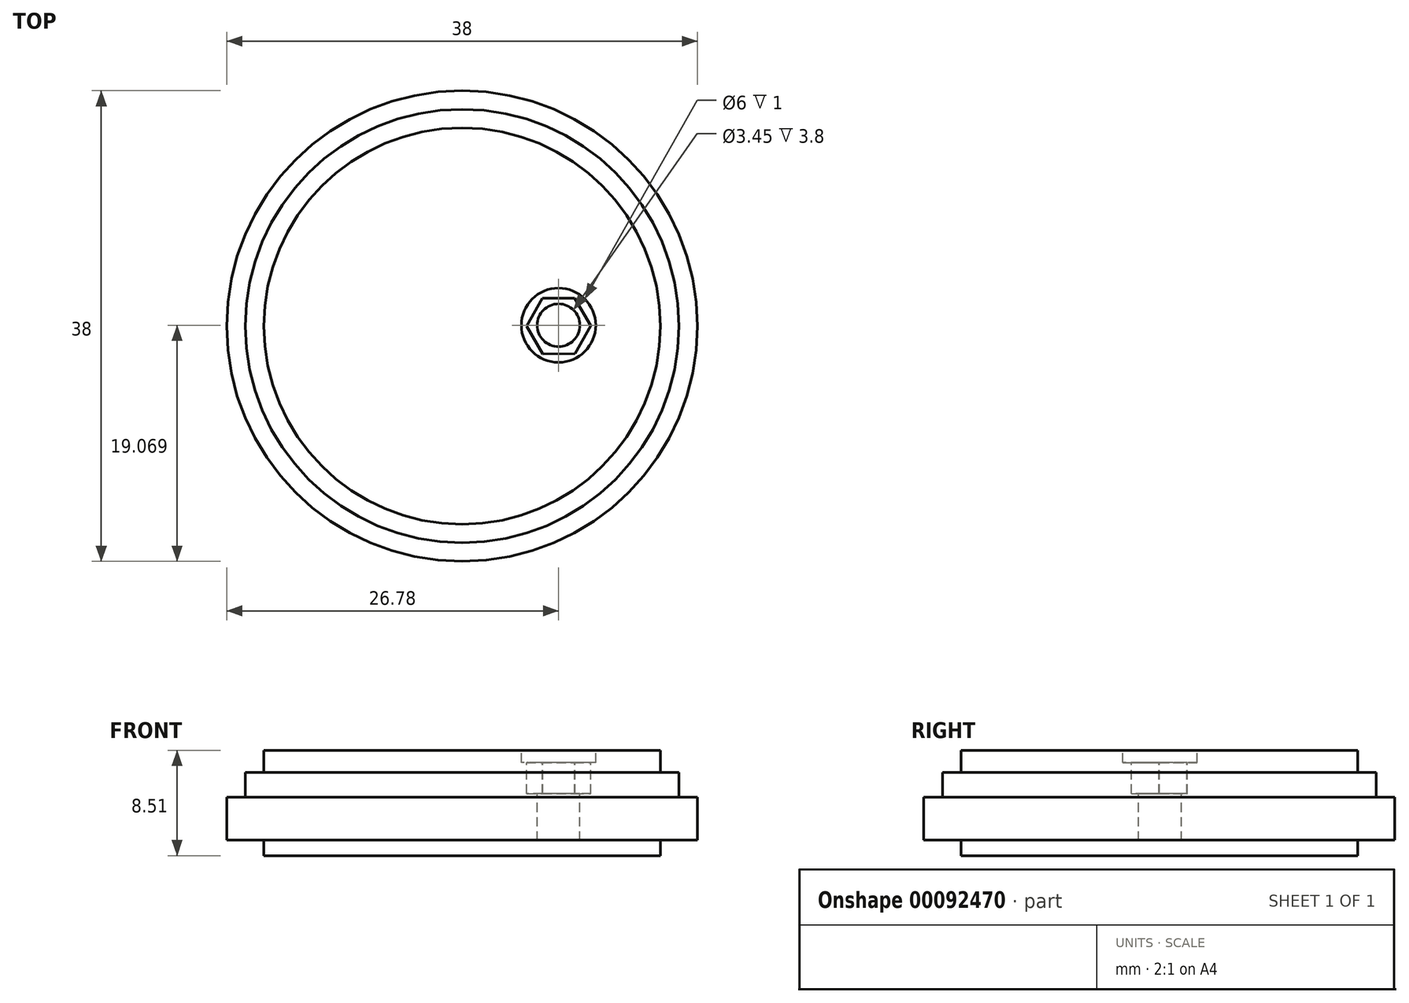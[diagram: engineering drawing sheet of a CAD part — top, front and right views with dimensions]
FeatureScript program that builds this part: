
annotation { "Feature Type Name" : "Feature", "Feature Type Description" : "" }
export const myFeature = defineFeature(function(context is Context, id is Id, definition is map)
    precondition{}
    {
        {
            var Q0;
            Q0=qCreatedBy(makeId("Front.planeOp"),FACE);
            var sketch = newSketch(context, id + "F0", { "sketchPlane" : qUnion([Q0])});
            skLineSegment(sketch, "E0", {"start": v(-26.8, 0) * mm, "end": v(11.2, 0) * mm});
            skLineSegment(sketch, "E1", {"start": v(11.2, 0) * mm, "end": v(11.2, 3.46) * mm});
            skLineSegment(sketch, "E2", {"start": v(11.2, 3.46) * mm, "end": v(9.7, 3.46) * mm});
            skLineSegment(sketch, "E3", {"start": v(9.7, 3.46) * mm, "end": v(9.7, 5.47) * mm});
            skLineSegment(sketch, "E4", {"start": v(9.7, 5.47) * mm, "end": v(8.2, 5.47) * mm});
            skLineSegment(sketch, "E5", {"start": v(8.2, 5.47) * mm, "end": v(8.2, 7.26) * mm});
            skLineSegment(sketch, "E6", {"start": v(8.2, 7.26) * mm, "end": v(-23.8, 7.26) * mm});
            skLineSegment(sketch, "E7", {"start": v(-23.8, 7.26) * mm, "end": v(-23.8, 5.47) * mm});
            skLineSegment(sketch, "E8", {"start": v(-23.8, 5.47) * mm, "end": v(-25.3, 5.47) * mm});
            skLineSegment(sketch, "E9", {"start": v(-25.3, 5.47) * mm, "end": v(-25.3, 3.46) * mm});
            skLineSegment(sketch, "E10", {"start": v(-25.3, 3.46) * mm, "end": v(-26.8, 3.46) * mm});
            skLineSegment(sketch, "E11", {"start": v(-26.8, 3.46) * mm, "end": v(-26.8, 0) * mm});
            skLineSegment(sketch, "E12", {"start": v(-23.8, 0) * mm, "end": v(-23.8, -1.25) * mm});
            skLineSegment(sketch, "E13", {"start": v(-23.8, -1.25) * mm, "end": v(8.2, -1.25) * mm});
            skLineSegment(sketch, "E14", {"start": v(8.2, -1.25) * mm, "end": v(8.2, 0) * mm});
            skLineSegment(sketch, "E15", {"start": v(-7.8, -4.04) * mm, "end": v(-7.8, 9.51) * mm});
            skPoint(sketch, "E15.startSnap0", {"position": v(-7.8, 0) * mm});
            skSolve(sketch);
        }
        {
            var Q0;
            {var subQ0=sQuery(id+"F0.wireOp",EDGE,"E1");Q0=makeQuery(id+"F0.imprint","IMPRINT",FACE,{"disambiguationData":[TD([[makeQuery(id+"F0.imprint","IMPRINT",EDGE,{"derivedFrom":subQ0}),1.0]])]});}
            var Q1;
            {var subQ0=sQuery(id+"F0.wireOp",EDGE,"E14");Q1=makeQuery(id+"F0.imprint","IMPRINT",FACE,{"disambiguationData":[TD([[makeQuery(id+"F0.imprint","IMPRINT",EDGE,{"derivedFrom":subQ0}),1.0]])]});}
            var Q2;
            Q2=sQuery(id+"F0.wireOp",EDGE,"E15");
            revolve(context, id + "F1", {"entities" : qUnion([Q0, Q1]), "axis" : qUnion([Q2]), "revolveType" : RevolveType.FULL});
        }
        {
            var Q0;
            Q0=makeQuery(id+"F1.opRevolve","SWEPT_FACE",FACE,{"disambiguationData":[OSD([sQuery(id+"F0.wireOp",EDGE,"E6")])]});
            cPlane(context, id + "F2", {"entities" : qUnion([Q0]), "cplaneType" : CPlaneType.OFFSET, "offset" : 0 * mm, "width" : 150 * mm, "height" : 150 * mm});
        }
        {
            var Q0;
            Q0=qCreatedBy(id+"F2.planeOp",FACE);
            var sketch = newSketch(context, id + "F3", { "sketchPlane" : qUnion([Q0])});
            skCircle(sketch, "E16", {"center": v(-0.01, 0.07) * mm, "radius": 3 * mm});
            skCircle(sketch, "E17", {"center": v(-0.01, 0.07) * mm, "radius": 1.73 * mm});
            skCircle(sketch, "E18.cCircle", {"center": v(0, 0) * mm, "radius": 2.25 * mm, "construction": true});
            skLineSegment(sketch, "E18.0", {"start": v(-2.6, -0.02) * mm, "end": v(-1.31, 2.24) * mm});
            skLineSegment(sketch, "E18.1", {"start": v(-1.31, 2.24) * mm, "end": v(1.28, 2.26) * mm});
            skLineSegment(sketch, "E18.2", {"start": v(1.28, 2.26) * mm, "end": v(2.6, 0.02) * mm});
            skLineSegment(sketch, "E18.3", {"start": v(2.6, 0.02) * mm, "end": v(1.31, -2.24) * mm});
            skLineSegment(sketch, "E18.4", {"start": v(1.31, -2.24) * mm, "end": v(-1.28, -2.26) * mm});
            skLineSegment(sketch, "E18.5", {"start": v(-1.28, -2.26) * mm, "end": v(-2.6, -0.02) * mm});
            skPoint(sketch, "E18.0.midPoint", {"position": v(-1.96, 1.11) * mm});
            skSolve(sketch);
        }
        {
            var Q0;
            Q0=makeQuery(id+"F3.imprint","IMPRINT",FACE,{"disambiguationData":[TD([[makeQuery(id+"F3.imprint","IMPRINT",EDGE,{"derivedFrom":sQuery(id+"F3.wireOp",EDGE,"E17")}),1.0]])]});
            extrude(context, id + "F4", {"entities" : qUnion([Q0]), "operationType" : NewBodyOperationType.REMOVE, "oppositeDirection" : true, "depth" : 7.3 * mm});
        }
        {
            var Q0;
            Q0=makeQuery(id+"F3.imprint","IMPRINT",FACE,{"disambiguationData":[TD([[makeQuery(id+"F3.imprint","IMPRINT",EDGE,{"derivedFrom":sQuery(id+"F3.wireOp",EDGE,"E17")}),-1.0]])]});
            extrude(context, id + "F5", {"entities" : qUnion([Q0]), "operationType" : NewBodyOperationType.REMOVE, "oppositeDirection" : true, "depth" : 3.5 * mm});
        }
        {
            var Q0;
            Q0=makeQuery(id+"F3.imprint","IMPRINT",FACE,{"disambiguationData":[TD([[makeQuery(id+"F3.imprint","IMPRINT",EDGE,{"derivedFrom":sQuery(id+"F3.wireOp",EDGE,"E16")}),1.0]])]});
            extrude(context, id + "F6", {"entities" : qUnion([Q0]), "operationType" : NewBodyOperationType.REMOVE, "oppositeDirection" : true, "depth" : 1 * mm});
        }
    });
